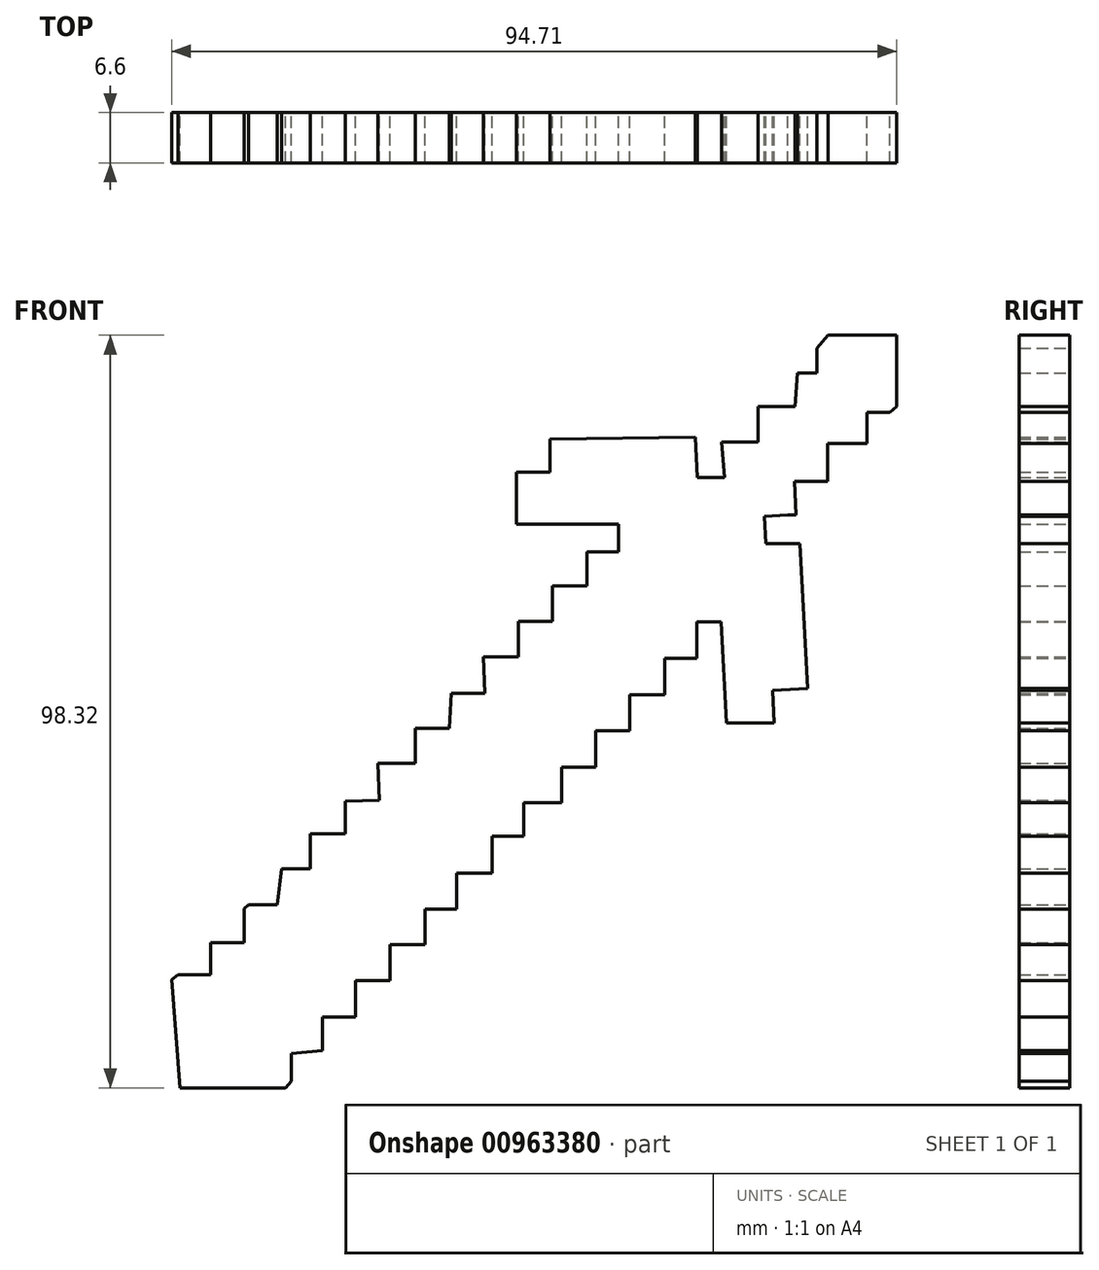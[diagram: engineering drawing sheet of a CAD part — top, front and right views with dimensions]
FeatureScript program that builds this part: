
annotation { "Feature Type Name" : "Feature", "Feature Type Description" : "" }
export const myFeature = defineFeature(function(context is Context, id is Id, definition is map)
    precondition{}
    {
        {
            var Q0;
            Q0=qCreatedBy(makeId("Front.planeOp"),FACE);
            var sketch = newSketch(context, id + "F0", { "sketchPlane" : qUnion([Q0])});
            skLineSegment(sketch, "E0", {"start": v(-34.77, -58.57) * mm, "end": v(-21, -58.57) * mm});
            skLineSegment(sketch, "E1", {"start": v(-21, -58.57) * mm, "end": v(-20.26, -57.7) * mm});
            skLineSegment(sketch, "E2", {"start": v(-20.26, -57.7) * mm, "end": v(-20.26, -54.08) * mm});
            skLineSegment(sketch, "E3", {"start": v(-20.26, -54.08) * mm, "end": v(-16.16, -53.69) * mm});
            skLineSegment(sketch, "E4", {"start": v(-16.16, -53.69) * mm, "end": v(-16.16, -49.3) * mm});
            skLineSegment(sketch, "E5", {"start": v(-16.16, -49.3) * mm, "end": v(-11.86, -49.3) * mm});
            skLineSegment(sketch, "E6", {"start": v(-11.86, -49.3) * mm, "end": v(-11.86, -44.55) * mm});
            skLineSegment(sketch, "E7", {"start": v(-11.86, -44.55) * mm, "end": v(-7.32, -44.55) * mm});
            skLineSegment(sketch, "E8", {"start": v(-7.32, -44.55) * mm, "end": v(-7.32, -39.87) * mm});
            skLineSegment(sketch, "E9", {"start": v(-7.32, -39.87) * mm, "end": v(-2.78, -39.87) * mm});
            skLineSegment(sketch, "E10", {"start": v(-2.78, -39.87) * mm, "end": v(-2.78, -35.22) * mm});
            skLineSegment(sketch, "E11", {"start": v(-2.78, -35.22) * mm, "end": v(1.33, -35.22) * mm});
            skLineSegment(sketch, "E12", {"start": v(1.33, -35.22) * mm, "end": v(1.33, -30.52) * mm});
            skLineSegment(sketch, "E13", {"start": v(1.33, -30.52) * mm, "end": v(5.96, -30.52) * mm});
            skLineSegment(sketch, "E14", {"start": v(5.96, -30.52) * mm, "end": v(5.96, -25.69) * mm});
            skLineSegment(sketch, "E15", {"start": v(5.96, -25.69) * mm, "end": v(10.1, -25.69) * mm});
            skLineSegment(sketch, "E16", {"start": v(10.1, -25.69) * mm, "end": v(10.1, -21.33) * mm});
            skLineSegment(sketch, "E17", {"start": v(10.1, -21.33) * mm, "end": v(15.07, -21.33) * mm});
            skLineSegment(sketch, "E18", {"start": v(15.07, -21.33) * mm, "end": v(15.07, -16.7) * mm});
            skLineSegment(sketch, "E19", {"start": v(15.07, -16.7) * mm, "end": v(19.5, -16.7) * mm});
            skLineSegment(sketch, "E20", {"start": v(19.5, -16.7) * mm, "end": v(19.5, -11.94) * mm});
            skLineSegment(sketch, "E21", {"start": v(19.5, -11.94) * mm, "end": v(23.99, -11.94) * mm});
            skLineSegment(sketch, "E22", {"start": v(23.99, -11.94) * mm, "end": v(23.99, -7.24) * mm});
            skLineSegment(sketch, "E23", {"start": v(23.99, -7.24) * mm, "end": v(28.54, -7.24) * mm});
            skLineSegment(sketch, "E24", {"start": v(28.54, -7.24) * mm, "end": v(28.54, -2.48) * mm});
            skLineSegment(sketch, "E25", {"start": v(28.54, -2.48) * mm, "end": v(32.69, -2.48) * mm});
            skLineSegment(sketch, "E26", {"start": v(32.69, -2.48) * mm, "end": v(32.69, 1.88) * mm});
            skLineSegment(sketch, "E27", {"start": v(32.69, 1.88) * mm, "end": v(32.69, 2.33) * mm});
            skLineSegment(sketch, "E28", {"start": v(32.69, 2.33) * mm, "end": v(35.88, 2.33) * mm});
            skLineSegment(sketch, "E29", {"start": v(35.88, 2.33) * mm, "end": v(36.56, -10.91) * mm});
            skLineSegment(sketch, "E30", {"start": v(36.56, -10.91) * mm, "end": v(42.82, -10.91) * mm});
            skLineSegment(sketch, "E31", {"start": v(42.82, -10.91) * mm, "end": v(42.6, -6.64) * mm});
            skLineSegment(sketch, "E32", {"start": v(42.6, -6.64) * mm, "end": v(47.18, -6.4) * mm});
            skLineSegment(sketch, "E33", {"start": v(47.18, -6.4) * mm, "end": v(46.2, 12.5) * mm});
            skLineSegment(sketch, "E34", {"start": v(46.2, 12.5) * mm, "end": v(41.71, 12.5) * mm});
            skLineSegment(sketch, "E35", {"start": v(41.71, 12.5) * mm, "end": v(41.52, 16.1) * mm});
            skLineSegment(sketch, "E36", {"start": v(41.52, 16.1) * mm, "end": v(44.6, 16.26) * mm});
            skLineSegment(sketch, "E37", {"start": v(44.6, 16.26) * mm, "end": v(45.7, 16.26) * mm});
            skLineSegment(sketch, "E38", {"start": v(45.7, 16.26) * mm, "end": v(45.46, 20.64) * mm});
            skLineSegment(sketch, "E39", {"start": v(45.46, 20.64) * mm, "end": v(49.3, 20.64) * mm});
            skLineSegment(sketch, "E40", {"start": v(49.3, 20.64) * mm, "end": v(49.82, 20.64) * mm});
            skLineSegment(sketch, "E41", {"start": v(49.82, 20.64) * mm, "end": v(49.82, 25.6) * mm});
            skLineSegment(sketch, "E42", {"start": v(49.82, 25.6) * mm, "end": v(54.93, 25.6) * mm});
            skLineSegment(sketch, "E43", {"start": v(54.93, 25.6) * mm, "end": v(54.93, 29.66) * mm});
            skLineSegment(sketch, "E44", {"start": v(54.93, 29.66) * mm, "end": v(57.95, 29.66) * mm});
            skLineSegment(sketch, "E45", {"start": v(57.95, 29.66) * mm, "end": v(58.82, 30.44) * mm});
            skLineSegment(sketch, "E46", {"start": v(58.82, 30.44) * mm, "end": v(58.82, 39.75) * mm});
            skLineSegment(sketch, "E47", {"start": v(58.82, 39.75) * mm, "end": v(49.87, 39.75) * mm});
            skLineSegment(sketch, "E48", {"start": v(49.87, 39.75) * mm, "end": v(48.42, 38.07) * mm});
            skLineSegment(sketch, "E49", {"start": v(48.42, 38.07) * mm, "end": v(48.42, 34.82) * mm});
            skLineSegment(sketch, "E50", {"start": v(48.42, 34.82) * mm, "end": v(45.84, 34.82) * mm});
            skLineSegment(sketch, "E51", {"start": v(45.84, 34.82) * mm, "end": v(45.54, 30.44) * mm});
            skLineSegment(sketch, "E52", {"start": v(45.54, 30.44) * mm, "end": v(40.74, 30.44) * mm});
            skLineSegment(sketch, "E53", {"start": v(40.74, 30.44) * mm, "end": v(40.74, 25.8) * mm});
            skLineSegment(sketch, "E54", {"start": v(40.74, 25.8) * mm, "end": v(35.94, 25.8) * mm});
            skLineSegment(sketch, "E55", {"start": v(35.94, 25.8) * mm, "end": v(36.34, 21.2) * mm});
            skLineSegment(sketch, "E56", {"start": v(36.34, 21.2) * mm, "end": v(32.78, 21.2) * mm});
            skLineSegment(sketch, "E57", {"start": v(32.78, 21.2) * mm, "end": v(32.5, 26.46) * mm});
            skLineSegment(sketch, "E58", {"start": v(32.5, 26.46) * mm, "end": v(13.55, 26.16) * mm});
            skLineSegment(sketch, "E59", {"start": v(13.55, 26.16) * mm, "end": v(13.55, 21.86) * mm});
            skLineSegment(sketch, "E60", {"start": v(13.55, 21.86) * mm, "end": v(9.17, 21.86) * mm});
            skLineSegment(sketch, "E61", {"start": v(9.17, 21.86) * mm, "end": v(9.17, 15.07) * mm});
            skLineSegment(sketch, "E62", {"start": v(9.17, 15.07) * mm, "end": v(22.48, 15.07) * mm});
            skLineSegment(sketch, "E63", {"start": v(22.48, 15.07) * mm, "end": v(22.48, 11.42) * mm});
            skLineSegment(sketch, "E64", {"start": v(22.48, 11.42) * mm, "end": v(18.4, 11.42) * mm});
            skLineSegment(sketch, "E65", {"start": v(18.4, 11.42) * mm, "end": v(18.4, 7) * mm});
            skLineSegment(sketch, "E66", {"start": v(18.4, 7) * mm, "end": v(13.85, 7) * mm});
            skLineSegment(sketch, "E67", {"start": v(13.85, 7) * mm, "end": v(13.85, 2.38) * mm});
            skLineSegment(sketch, "E68", {"start": v(13.85, 2.38) * mm, "end": v(9.4, 2.38) * mm});
            skLineSegment(sketch, "E69", {"start": v(9.4, 2.38) * mm, "end": v(9.4, -2.3) * mm});
            skLineSegment(sketch, "E70", {"start": v(9.4, -2.3) * mm, "end": v(4.82, -2.3) * mm});
            skLineSegment(sketch, "E71", {"start": v(4.82, -2.3) * mm, "end": v(5.04, -7.02) * mm});
            skLineSegment(sketch, "E72", {"start": v(5.04, -7.02) * mm, "end": v(0.65, -7.02) * mm});
            skLineSegment(sketch, "E73", {"start": v(0.65, -7.02) * mm, "end": v(0.39, -11.58) * mm});
            skLineSegment(sketch, "E74", {"start": v(0.39, -11.58) * mm, "end": v(-4.06, -11.58) * mm});
            skLineSegment(sketch, "E75", {"start": v(-4.06, -11.58) * mm, "end": v(-4.06, -16.15) * mm});
            skLineSegment(sketch, "E76", {"start": v(-4.06, -16.15) * mm, "end": v(-8.9, -16.15) * mm});
            skLineSegment(sketch, "E77", {"start": v(-8.9, -16.15) * mm, "end": v(-8.75, -21.01) * mm});
            skLineSegment(sketch, "E78", {"start": v(-8.75, -21.01) * mm, "end": v(-13.2, -21.16) * mm});
            skLineSegment(sketch, "E79", {"start": v(-13.2, -21.16) * mm, "end": v(-13.2, -25.4) * mm});
            skLineSegment(sketch, "E80", {"start": v(-13.2, -25.4) * mm, "end": v(-17.74, -25.4) * mm});
            skLineSegment(sketch, "E81", {"start": v(-17.74, -25.4) * mm, "end": v(-17.74, -29.94) * mm});
            skLineSegment(sketch, "E82", {"start": v(-17.74, -29.94) * mm, "end": v(-21.5, -29.94) * mm});
            skLineSegment(sketch, "E83", {"start": v(-21.5, -29.94) * mm, "end": v(-22.06, -34.65) * mm});
            skLineSegment(sketch, "E84", {"start": v(-22.06, -34.65) * mm, "end": v(-25.82, -34.65) * mm});
            skLineSegment(sketch, "E85", {"start": v(-25.82, -34.65) * mm, "end": v(-26.38, -35.16) * mm});
            skLineSegment(sketch, "E86", {"start": v(-26.38, -35.16) * mm, "end": v(-26.38, -39.64) * mm});
            skLineSegment(sketch, "E87", {"start": v(-26.38, -39.64) * mm, "end": v(-30.2, -39.64) * mm});
            skLineSegment(sketch, "E88", {"start": v(-30.2, -39.64) * mm, "end": v(-30.78, -39.64) * mm});
            skLineSegment(sketch, "E89", {"start": v(-30.78, -39.64) * mm, "end": v(-30.78, -43.8) * mm});
            skLineSegment(sketch, "E90", {"start": v(-30.78, -43.8) * mm, "end": v(-35.02, -43.8) * mm});
            skLineSegment(sketch, "E91", {"start": v(-35.02, -43.8) * mm, "end": v(-35.9, -44.43) * mm});
            skLineSegment(sketch, "E92", {"start": v(-35.9, -44.43) * mm, "end": v(-34.77, -58.57) * mm});
            skSolve(sketch);
        }
        {
            var Q0;
            Q0 = qSketchRegion(id + "F0", true);
            extrude(context, id + "F1", {"entities" : qUnion([Q0]), "depth" : 6.6 * mm, "offsetDistance" : 25.4 * mm});
        }
    });
